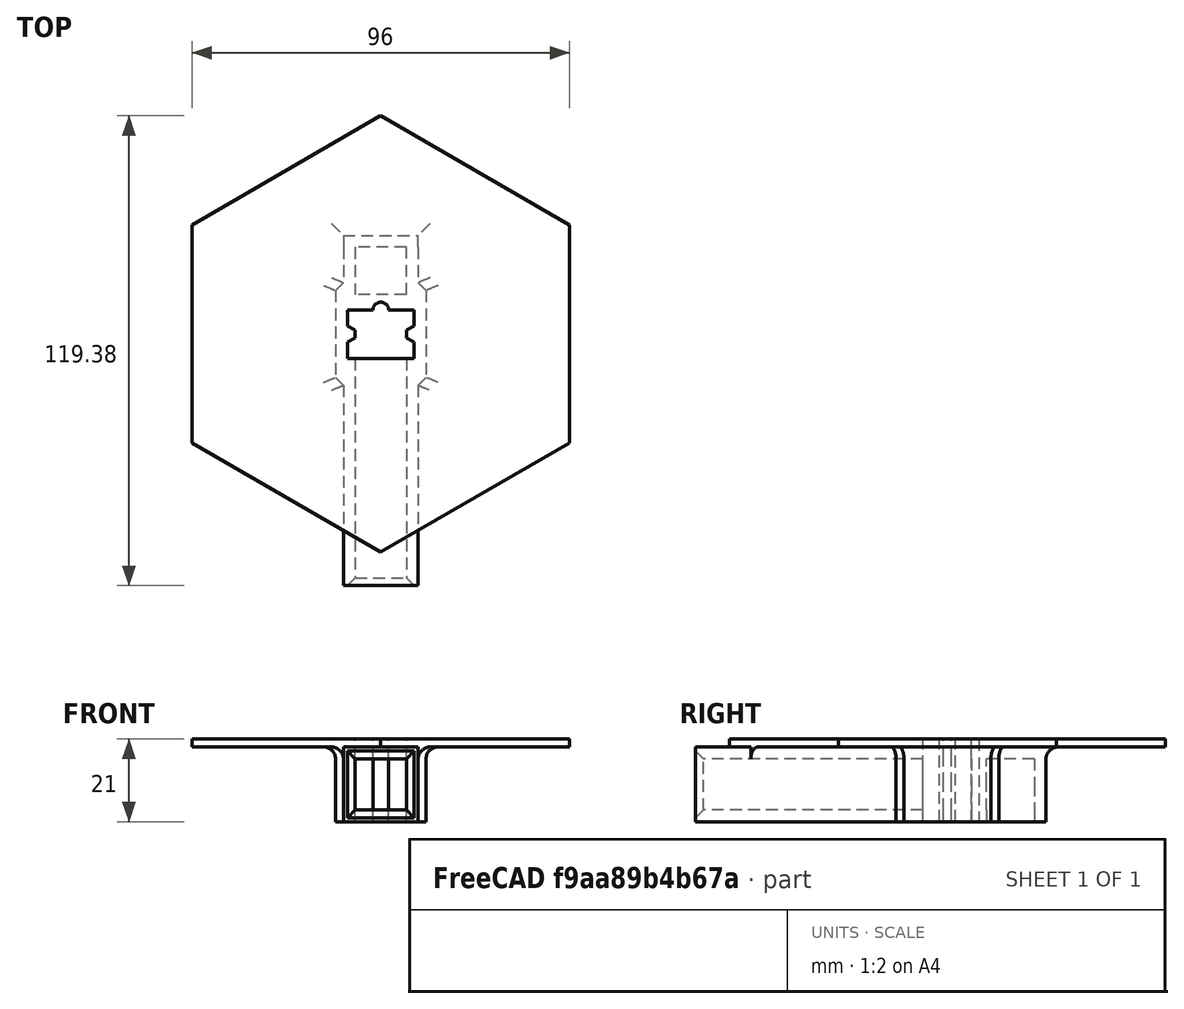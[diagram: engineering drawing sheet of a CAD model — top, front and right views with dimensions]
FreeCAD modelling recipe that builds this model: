
FCSTD DOCUMENT  (FreeCAD 0.21R33771 (Git))
Label: holder
License: All rights reserved
LicenseURL: http://en.wikipedia.org/wiki/All_rights_reserved
objects: Sketcher::SketchObject×7, PartDesign::Pad×5, PartDesign::Pocket×4, Spreadsheet::Sheet×1, PartDesign::Chamfer×1, PartDesign::Fillet×1, PartDesign::Body×1, Mesh::Feature×1
note: 30 computed .brp shape members not serialized (recipe doc carries the construction recipe); baked Part::Feature solids carry a one-line shape summary decoded from their .brp

FEATURE [Sketcher::SketchObject] Sketch
  FullyConstrained = true
  MapMode = 5
  Placement = pos=(0,0,0) rot=(1,0,0;1.5708rad)
  expr: Constraints[25] = Spreadsheet.B1
  sketch-geometry (14):
    g0: LineSegment StartX=-6.5 StartY=6.5 StartZ=0 EndX=6.5 EndY=6.5 EndZ=0
    g1: LineSegment StartX=6.5 StartY=6.5 StartZ=0 EndX=6.5 EndY=-6.5 EndZ=0
    g2: LineSegment StartX=6.5 StartY=-6.5 StartZ=0 EndX=-6.5 EndY=-6.5 EndZ=0
    g3: LineSegment StartX=-6.5 StartY=-6.5 StartZ=0 EndX=-6.5 EndY=6.5 EndZ=0
    g4: LineSegment StartX=-6 StartY=6 StartZ=0 EndX=6 EndY=6 EndZ=0
    g5: LineSegment StartX=6 StartY=6 StartZ=0 EndX=6 EndY=-6 EndZ=0
    g6: LineSegment StartX=6 StartY=-6 StartZ=0 EndX=-6 EndY=-6 EndZ=0
    g7: LineSegment StartX=-6 StartY=-6 StartZ=0 EndX=-6 EndY=6 EndZ=0
    g8: LineSegment StartX=-9.5 StartY=9.5 StartZ=0 EndX=9.5 EndY=9.5 EndZ=0
    g9: LineSegment StartX=9.5 StartY=9.5 StartZ=0 EndX=9.5 EndY=-9.5 EndZ=0
    g10: LineSegment StartX=9.5 StartY=-9.5 StartZ=0 EndX=-9.5 EndY=-9.5 EndZ=0
    g11: LineSegment StartX=-9.5 StartY=-9.5 StartZ=0 EndX=-9.5 EndY=9.5 EndZ=0
    g12: LineSegment StartX=-9.5 StartY=9.5 StartZ=0 EndX=9.5 EndY=-9.5 EndZ=0
    g13: LineSegment StartX=-9.5 StartY=-9.5 StartZ=0 EndX=9.5 EndY=9.5 EndZ=0
  constraints (40):
    c: Coincident(g0,g1)
    c: Coincident(g1,g2)
    c: Coincident(g2,g3)
    c: Coincident(g3,g0)
    c: Horizontal(g0)
    c: Horizontal(g2)
    c: Vertical(g1)
    c: Vertical(g3)
    c: Coincident(g4,g5)
    c: Coincident(g5,g6)
    c: Coincident(g6,g7)
    c: Coincident(g7,g4)
    c: Horizontal(g4)
    c: Horizontal(g6)
    c: Vertical(g5)
    c: Vertical(g7)
    c: Coincident(g8,g9)
    c: Coincident(g9,g10)
    c: Coincident(g10,g11)
    c: Coincident(g11,g8)
    c: Horizontal(g8)
    c: Horizontal(g10)
    c: Vertical(g9)
    c: Vertical(g11)
    c: Equal(g4,g7)
    c: Distance(g4) = 12
    c: Coincident(g12,g8)
    c: Coincident(g12,g9)
    c: PointOnObject(g-1,g12)
    c: PointOnObject(g4,g12)
    c: PointOnObject(g0,g12)
    c: PointOnObject(g5,g12)
    c: PointOnObject(g1,g12)
    c: Distance(g4,g0) = 0.5
    c: Coincident(g13,g10)
    c: Coincident(g13,g8)
    c: PointOnObject(g0,g13)
    c: PointOnObject(g4,g13)
    c: PointOnObject(g-1,g13)
    c: Distance(g0,g8) = 3
FEATURE [Spreadsheet::Sheet] Spreadsheet
  cells = A1='magnet width [mm]; B1=12
FEATURE [PartDesign::Pad] Pad
  Direction = (0,-1,2e-16)
  Length = 86
  Length2 = 10
  Placement = pos=(0,0,0) rot=(1,0,0;1.5708rad)
  Profile = -> Sketch
  ReferenceAxis = -> Sketch [N_Axis]
  Type = 0
  expr: Length = Spreadsheet.B1 * 7 + 2 * 1
FEATURE [Sketcher::SketchObject] Sketch001
  ExternalGeometry = -> [Pad]
  FullyConstrained = true
  MapMode = 5
  Placement = pos=(0,0,0) rot=(1,0,0;1.5708rad)
  Support = -> [XZ_Plane001]
  sketch-geometry (4):
    g0: LineSegment StartX=-9.5 StartY=9.5 StartZ=0 EndX=9.5 EndY=9.5 EndZ=0
    g1: LineSegment StartX=9.5 StartY=9.5 StartZ=0 EndX=9.5 EndY=-9.5 EndZ=0
    g2: LineSegment StartX=9.5 StartY=-9.5 StartZ=0 EndX=-9.5 EndY=-9.5 EndZ=0
    g3: LineSegment StartX=-9.5 StartY=-9.5 StartZ=0 EndX=-9.5 EndY=9.5 EndZ=0
  constraints (10):
    c: Coincident(g0,g1)
    c: Coincident(g1,g2)
    c: Coincident(g2,g3)
    c: Coincident(g3,g0)
    c: Horizontal(g0)
    c: Horizontal(g2)
    c: Vertical(g1)
    c: Vertical(g3)
    c: Coincident(g0,g-4)
    c: Coincident(g1,g-6)
FEATURE [PartDesign::Pad] Pad001
  BaseFeature = -> Pad
  Direction = (0,-1,-2e-16)
  Length = 3
  Length2 = 10
  Placement = pos=(0,0,0) rot=(1,0,0;1.5708rad)
  Profile = -> Sketch001
  ReferenceAxis = -> Sketch001 [N_Axis]
  Reversed = true
  Type = 0
FEATURE [PartDesign::Pad] Pad002
  BaseFeature = -> Pad001
  Direction = (0,-1,-2e-16)
  Length = 16
  Length2 = -12.1
  Placement = pos=(0,0,0) rot=(1,0,0;1.5708rad)
  Profile = -> Sketch001
  ReferenceAxis = -> Sketch001 [N_Axis]
  Type = 4
  expr: Length = Spreadsheet.B1 + 2 + 2
  expr: Length2 = -(Spreadsheet.B1 + 0.1)
FEATURE [Sketcher::SketchObject] Sketch002
  ExternalGeometry = -> [Pad002]
  FullyConstrained = true
  MapMode = 5
  Support = -> [XY_Plane001]
  sketch-geometry (4):
    g0: LineSegment StartX=-6.5 StartY=0 StartZ=0 EndX=6.5 EndY=0 EndZ=0
    g1: LineSegment StartX=6.5 StartY=0 StartZ=0 EndX=6.5 EndY=-12.1 EndZ=0
    g2: LineSegment StartX=6.5 StartY=-12.1 StartZ=0 EndX=-6.5 EndY=-12.1 EndZ=0
    g3: LineSegment StartX=-6.5 StartY=-12.1 StartZ=0 EndX=-6.5 EndY=0 EndZ=0
  constraints (10):
    c: Coincident(g0,g1)
    c: Coincident(g1,g2)
    c: Coincident(g2,g3)
    c: Coincident(g3,g0)
    c: Horizontal(g0)
    c: Vertical(g1)
    c: Vertical(g3)
    c: PointOnObject(g0,g-1)
    c: Coincident(g2,g-4)
    c: Coincident(g1,g-3)
FEATURE [PartDesign::Pocket] Pocket
  BaseFeature = -> Pad002
  Direction = (0,0,-1)
  Length = 16
  Length2 = 5
  Placement = pos=(0,0,0) rot=(1,0,0;1.5708rad)
  Profile = -> Sketch002
  ReferenceAxis = -> Sketch002 [N_Axis]
  Type = 1
FEATURE [Sketcher::SketchObject] Sketch003
  ExternalGeometry = -> [Pocket]
  FullyConstrained = true
  MapMode = 5
  Support = -> [XY_Plane001]
  sketch-geometry (7):
    g0: LineSegment StartX=-6.5 StartY=-16 StartZ=0 EndX=6.5 EndY=-16 EndZ=0
    g1: LineSegment StartX=6.5 StartY=-16 StartZ=0 EndX=6.5 EndY=-29 EndZ=0
    g2: LineSegment StartX=6.5 StartY=-29 StartZ=0 EndX=-6.5 EndY=-29 EndZ=0
    g3: LineSegment StartX=-6.5 StartY=-29 StartZ=0 EndX=-6.5 EndY=-16 EndZ=0
    g4: LineSegment StartX=-6.5 StartY=-28.1 StartZ=0 EndX=6.5 EndY=-28.1 EndZ=0
    g5: LineSegment StartX=-6.5 StartY=-16 StartZ=0 EndX=-6.5 EndY=-28.1 EndZ=0
    g6: LineSegment StartX=6.5 StartY=-16 StartZ=0 EndX=6.5 EndY=-28.1 EndZ=0
  constraints (19):
    c: Coincident(g0,g1)
    c: Coincident(g1,g2)
    c: Coincident(g2,g3)
    c: Coincident(g3,g0)
    c: Horizontal(g0)
    c: Horizontal(g2)
    c: Vertical(g1)
    c: Vertical(g3)
    c: Coincident(g0,g-4)
    c: PointOnObject(g1,g-5)
    c: Equal(g1,g0)
    c: PointOnObject(g4,g3)
    c: PointOnObject(g4,g1)
    c: Horizontal(g4)
    c: Distance(g0,g4) = 12.1
    c: Coincident(g5,g0)
    c: Coincident(g5,g4)
    c: Coincident(g6,g0)
    c: Coincident(g6,g4)
FEATURE [PartDesign::Pocket] Pocket001
  BaseFeature = -> Pocket
  Direction = (0,0,-1)
  Length = 11
  Length2 = 5
  Placement = pos=(0,0,0) rot=(1,0,0;1.5708rad)
  Profile = -> Sketch003
  ReferenceAxis = -> Sketch003 [N_Axis]
  Type = 1
FEATURE [Sketcher::SketchObject] Sketch004
  ExternalGeometry = -> [Pocket001]
  FullyConstrained = true
  MapMode = 5
  Placement = pos=(0,1e-15,9.5) rot=(0,0,1;3.14159rad)
  Support = -> [Pocket001]
  expr: Constraints[18] = Spreadsheet.B1 * 4
  sketch-geometry (9):
    g0: LineSegment StartX=0 StartY=-33.3756 StartZ=0 EndX=48 EndY=-5.66281 EndZ=0
    g1: LineSegment StartX=48 StartY=-5.66281 StartZ=0 EndX=48 EndY=49.7628 EndZ=0
    g2: LineSegment StartX=48 StartY=49.7628 StartZ=0 EndX=-4.9596e-12 EndY=77.4756 EndZ=0
    g3: LineSegment StartX=-4.9596e-12 StartY=77.4756 StartZ=0 EndX=-48 EndY=49.7628 EndZ=0
    g4: LineSegment StartX=-48 StartY=49.7628 StartZ=0 EndX=-48 EndY=-5.66281 EndZ=0
    g5: LineSegment StartX=-48 StartY=-5.66281 StartZ=0 EndX=0 EndY=-33.3756 EndZ=0
    g6: Circle CenterX=0 CenterY=22.05 CenterZ=0 NormalX=0 NormalY=0 NormalZ=1 AngleXU=0 Radius=55.4256
    g7: LineSegment StartX=-6.5 StartY=28.1 StartZ=0 EndX=6.5 EndY=16 EndZ=0
    g8: GeomPoint X=0 Y=22.05 Z=0
  constraints (20):
    c: Coincident(g0,g1)
    c: Coincident(g1,g2)
    c: Coincident(g2,g3)
    c: Coincident(g3,g4)
    c: Coincident(g4,g5)
    c: Coincident(g5,g0)
    c: Equal(g0, g1-g5) x5
    c: PointOnObject(g0,g6)
    c: PointOnObject(g1,g6)
    c: PointOnObject(g2,g6)
    c: PointOnObject(g3,g6)
    c: PointOnObject(g4,g6)
    c: PointOnObject(g5,g6)
    c: PointOnObject(g5,g-2)
    c: Distance(g6,g4) = 48
    c: Coincident(g7,g-4)
    c: PointOnObject(g8,g-2)
    c: PointOnObject(g8,g7)
    c: Coincident(g6,g8)
    c: Coincident(g-3,g7)
FEATURE [PartDesign::Pad] Pad003
  BaseFeature = -> Pocket001
  Direction = (0,3e-16,1)
  Length = 2
  Length2 = 10
  Placement = pos=(0,0,0) rot=(1,0,0;1.5708rad)
  Profile = -> Sketch004
  ReferenceAxis = -> Sketch004 [N_Axis]
  Type = 0
FEATURE [PartDesign::Pocket] Pocket002
  BaseFeature = -> Pad003
  Direction = (0,0,-1)
  Length = 5
  Length2 = 5
  Placement = pos=(0,0,0) rot=(1,0,0;1.5708rad)
  Profile = -> Sketch003
  ReferenceAxis = -> Sketch003 [N_Axis]
  Reversed = true
  Type = 1
FEATURE [PartDesign::Chamfer] Chamfer
  Angle = 45
  Base = -> Pocket002 [Edge80,Edge81,Edge83,Edge82]
  BaseFeature = -> Pocket002
  ChamferType = 0
  FlipDirection = false
  Placement = pos=(0,0,0) rot=(1,0,0;1.5708rad)
  Size = 2
  Size2 = 1
  SupportTransform = false
  UseAllEdges = false
FEATURE [Sketcher::SketchObject] Sketch005
  ExternalGeometry = -> [Chamfer]
  FullyConstrained = false
  MapMode = 5
  Placement = pos=(0,-1e-15,-9.5) rot=(1,0,0;3.14159rad)
  Support = -> [Chamfer]
  sketch-geometry (41):
    g0: LineSegment StartX=-6.5 StartY=28.1 StartZ=0 EndX=6.5 EndY=16 EndZ=0
    g1: LineSegment StartX=-6.5 StartY=16 StartZ=0 EndX=6.5 EndY=28.1 EndZ=0
    g2: GeomPoint X=1.7e-15 Y=22.05 Z=0
    g3: LineSegment StartX=1.7e-15 StartY=22.05 StartZ=0 EndX=-6.5 EndY=22.05 EndZ=0
    g4: LineSegment StartX=1.7e-15 StartY=22.05 StartZ=0 EndX=6.5 EndY=22.05 EndZ=0
    g5: LineSegment StartX=1.7e-15 StartY=22.05 StartZ=0 EndX=1.7e-15 EndY=16 EndZ=0
    g6: Circle CenterX=1.7e-15 CenterY=16 CenterZ=0 NormalX=0 NormalY=0 NormalZ=1 AngleXU=0 Radius=2
    g7: LineSegment StartX=-9.5 StartY=16 StartZ=0 EndX=-6.5 EndY=16 EndZ=0
    g8: LineSegment StartX=-8.5 StartY=16 StartZ=0 EndX=8.5 EndY=16 EndZ=0
    g9: LineSegment StartX=8.5 StartY=16 StartZ=0 EndX=8.5 EndY=28.3 EndZ=0
    g10: LineSegment StartX=8.5 StartY=28.3 StartZ=0 EndX=-8.5 EndY=28.3 EndZ=0
    g11: LineSegment StartX=-8.5 StartY=28.3 StartZ=0 EndX=-8.5 EndY=16 EndZ=0
    g12: LineSegment StartX=-6.5 StartY=22.05 StartZ=0 EndX=-8.5 EndY=22.05 EndZ=0
    g13: LineSegment StartX=6.5 StartY=22.05 StartZ=0 EndX=8.5 EndY=22.05 EndZ=0
    g14: LineSegment StartX=6.5 StartY=28.1 StartZ=0 EndX=6.5 EndY=28.3 EndZ=0
    g15: LineSegment StartX=1.7e-15 StartY=16 StartZ=0 EndX=-1.65657 EndY=17.1206 EndZ=0
    g16: Circle CenterX=-6.5 CenterY=22.05 CenterZ=0 NormalX=0 NormalY=0 NormalZ=1 AngleXU=0 Radius=1
    g17: Circle CenterX=6.5 CenterY=22.05 CenterZ=0 NormalX=0 NormalY=0 NormalZ=1 AngleXU=0 Radius=1
    g18: GeomPoint X=-6.5 Y=23.05 Z=0
    g19: GeomPoint X=6.5 Y=23.05 Z=0
    g20: GeomPoint X=-6.5 Y=21.05 Z=0
    g21: GeomPoint X=6.5 Y=21.05 Z=0
    g22: Circle CenterX=-8.5 CenterY=22.05 CenterZ=0 NormalX=0 NormalY=0 NormalZ=1 AngleXU=0 Radius=2
    g23: Circle CenterX=8.5 CenterY=22.05 CenterZ=0 NormalX=0 NormalY=0 NormalZ=1 AngleXU=0 Radius=2
    g24: GeomPoint X=-8.5 Y=24.05 Z=0
    g25: GeomPoint X=-8.5 Y=20.05 Z=0
    g26: GeomPoint X=8.5 Y=24.05 Z=0
    g27: GeomPoint X=8.5 Y=20.05 Z=0
    g28: LineSegment StartX=-8.5 StartY=24.05 StartZ=0 EndX=-6.5 EndY=23.05 EndZ=0
    g29: LineSegment StartX=-6.5 StartY=21.05 StartZ=0 EndX=-8.5 EndY=20.05 EndZ=0
    g30: LineSegment StartX=-8.5 StartY=28.3 StartZ=0 EndX=-8.5 EndY=24.05 EndZ=0
    g31: LineSegment StartX=-8.5 StartY=20.05 StartZ=0 EndX=-8.5 EndY=16 EndZ=0
    g32: LineSegment StartX=6.5 StartY=23.05 StartZ=0 EndX=8.5 EndY=24.05 EndZ=0
    g33: LineSegment StartX=6.5 StartY=21.05 StartZ=0 EndX=8.5 EndY=20.05 EndZ=0
    g34: LineSegment StartX=6.5 StartY=23.05 StartZ=0 EndX=6.5 EndY=21.05 EndZ=0
    g35: LineSegment StartX=-6.5 StartY=23.05 StartZ=0 EndX=-6.5 EndY=21.05 EndZ=0
    g36: LineSegment StartX=8.5 StartY=24.05 StartZ=0 EndX=8.5 EndY=28.3 EndZ=0
    g37: LineSegment StartX=8.5 StartY=20.05 StartZ=0 EndX=8.5 EndY=16 EndZ=0
    g38: LineSegment StartX=-8.5 StartY=16 StartZ=0 EndX=-2 EndY=16 EndZ=0
    g39: LineSegment StartX=2 StartY=16 StartZ=0 EndX=8.5 EndY=16 EndZ=0
    g40: ArcOfCircle CenterX=1.7e-15 CenterY=16 CenterZ=0 NormalX=0 NormalY=0 NormalZ=1 AngleXU=0 Radius=2 StartAngle=3.14159 EndAngle=6.28319
  constraints (95):
    c: PointOnObject(g2,g0)
    c: PointOnObject(g2,g1)
    c: Coincident(g3,g2)
    c: PointOnObject(g3,g-5)
    c: Horizontal(g3)
    c: Coincident(g4,g2)
    c: PointOnObject(g4,g-7)
    c: Horizontal(g4)
    c: Coincident(g5,g2)
    c: PointOnObject(g5,g-8)
    c: Vertical(g5)
    c: Coincident(g6,g5)
    c: Coincident(g7,g-3)
    c: Coincident(g7,g1)
    c: Coincident(g8,g9)
    c: Coincident(g9,g10)
    c: Coincident(g10,g11)
    c: Coincident(g11,g8)
    c: Horizontal(g8)
    c: Horizontal(g10)
    c: Vertical(g9)
    c: Vertical(g11)
    c: PointOnObject(g8,g7)
    c: Coincident(g12,g3)
    c: PointOnObject(g12,g11)
    c: Horizontal(g12)
    c: Coincident(g13,g4)
    c: PointOnObject(g13,g9)
    c: Horizontal(g13)
    c: Coincident(g14,g1)
    c: PointOnObject(g14,g10)
    c: Vertical(g14)
    c: Radius(g6) = 2
    c: Coincident(g0,g-8)
    c: Coincident(g1,g-7)
    c: Coincident(g0,g-6)
    c: Coincident(g1,g-8)
    c: Coincident(g15,g6)
    c: PointOnObject(g15,g6)
    c: Equal(g12,g13)
    c: Equal(g13,g15)
    c: Distance(g14) = 0.2
    c: Coincident(g16,g3)
    c: Coincident(g17,g4)
    c: Radius(g17) = 1
    c: Radius(g16) = 1
    c: PointOnObject(g18,g-5)
    c: PointOnObject(g19,g-7)
    c: PointOnObject(g20,g-5)
    c: PointOnObject(g21,g-7)
    c: PointOnObject(g18,g16)
    c: PointOnObject(g20,g16)
    c: PointOnObject(g21,g17)
    c: PointOnObject(g19,g17)
    c: Coincident(g22,g12)
    c: Coincident(g23,g13)
    c: Equal(g22,g23)
    c: Equal(g23,g6)
    c: PointOnObject(g24,g22)
    c: PointOnObject(g25,g22)
    c: PointOnObject(g26,g23)
    c: PointOnObject(g27,g23)
    c: PointOnObject(g26,g9)
    c: PointOnObject(g27,g9)
    c: PointOnObject(g24,g11)
    c: PointOnObject(g25,g11)
    c: Coincident(g28,g24)
    c: Coincident(g28,g18)
    c: Coincident(g29,g20)
    c: Coincident(g29,g25)
    c: Coincident(g30,g10)
    c: Coincident(g30,g28)
    c: Coincident(g31,g29)
    c: Coincident(g31,g8)
    c: Coincident(g32,g19)
    c: Coincident(g32,g26)
    c: Coincident(g33,g21)
    c: Coincident(g33,g27)
    c: Coincident(g34,g32)
    c: Coincident(g34,g33)
    c: Coincident(g35,g28)
    c: Coincident(g35,g29)
    c: Coincident(g36,g32)
    c: Coincident(g36,g10)
    c: Coincident(g37,g33)
    c: Coincident(g37,g8)
    c: Coincident(g38,g31)
    c: PointOnObject(g38,g6)
    c: PointOnObject(g39,g6)
    c: Coincident(g39,g37)
    c: Horizontal(g38)
    c: Horizontal(g39)
    c: Coincident(g40,g5)
    c: Coincident(g40,g38)
    c: PointOnObject(g40,g8)
FEATURE [Sketcher::SketchObject] Sketch006
  ExternalGeometry = -> [Chamfer]
  FullyConstrained = false
  MapMode = 5
  Placement = pos=(0,-1e-15,-9.5) rot=(1,0,0;3.14159rad)
  Support = -> [Chamfer]
  sketch-geometry (32):
    g0: Circle CenterX=-6.5 CenterY=16 CenterZ=0 NormalX=0 NormalY=0 NormalZ=1 AngleXU=0 Radius=5
    g1: Circle CenterX=6.5 CenterY=16 CenterZ=0 NormalX=0 NormalY=0 NormalZ=1 AngleXU=0 Radius=5
    g2: Circle CenterX=6.5 CenterY=28.1 CenterZ=0 NormalX=0 NormalY=0 NormalZ=1 AngleXU=0 Radius=5
    g3: Circle CenterX=-6.5 CenterY=28.1 CenterZ=0 NormalX=0 NormalY=0 NormalZ=1 AngleXU=0 Radius=5
    g4: LineSegment StartX=-6.5 StartY=16 StartZ=0 EndX=-6.5 EndY=11 EndZ=0
    g5: LineSegment StartX=6.5 StartY=16 StartZ=0 EndX=6.5 EndY=11 EndZ=0
    g6: LineSegment StartX=-6.5 StartY=11 StartZ=0 EndX=-9.5 EndY=11 EndZ=0
    g7: LineSegment StartX=6.5 StartY=11 StartZ=0 EndX=9.5 EndY=11 EndZ=0
    g8: LineSegment StartX=-6.5 StartY=28.1 StartZ=0 EndX=-6.5 EndY=33.1 EndZ=0
    g9: LineSegment StartX=6.5 StartY=28.1 StartZ=0 EndX=6.5 EndY=33.1 EndZ=0
    g10: LineSegment StartX=6.5 StartY=33.1 StartZ=0 EndX=9.5 EndY=33.1 EndZ=0
    g11: LineSegment StartX=-6.5 StartY=33.1 StartZ=0 EndX=-9.5 EndY=33.1 EndZ=0
    g12: LineSegment StartX=-9.5 StartY=11 StartZ=0 EndX=-11.5 EndY=11 EndZ=0
    g13: LineSegment StartX=-11.5 StartY=11 StartZ=0 EndX=-11.5 EndY=33.1 EndZ=0
    g14: LineSegment StartX=-11.5 StartY=33.1 StartZ=0 EndX=-9.5 EndY=33.1 EndZ=0
    g15: LineSegment StartX=-9.5 StartY=33.1 StartZ=0 EndX=-9.5 EndY=11 EndZ=0
    g16: LineSegment StartX=-6.5 StartY=28.1 StartZ=0 EndX=-11.5 EndY=28.1 EndZ=0
    g17: LineSegment StartX=6.5 StartY=28.1 StartZ=0 EndX=11.5 EndY=28.1 EndZ=0
    g18: LineSegment StartX=11.5 StartY=11 StartZ=0 EndX=11.5 EndY=33.1 EndZ=0
    g19: LineSegment StartX=11.5 StartY=33.1 StartZ=0 EndX=9.5 EndY=33.1 EndZ=0
    g20: LineSegment StartX=9.5 StartY=33.1 StartZ=0 EndX=9.5 EndY=11 EndZ=0
    g21: LineSegment StartX=-9.5 StartY=11 StartZ=0 EndX=-9.5 EndY=9 EndZ=0
    g22: LineSegment StartX=9.5 StartY=11 StartZ=0 EndX=9.5 EndY=9 EndZ=0
    g23: LineSegment StartX=9.5 StartY=9 StartZ=0 EndX=11.5 EndY=11 EndZ=0
    g24: LineSegment StartX=-11.5 StartY=11 StartZ=0 EndX=-9.5 EndY=9 EndZ=0
    g25: LineSegment StartX=9.5 StartY=9 StartZ=0 EndX=9.5 EndY=11 EndZ=0
    g26: LineSegment StartX=9.5 StartY=11 StartZ=0 EndX=11.5 EndY=11 EndZ=0
    g27: LineSegment StartX=-9.5 StartY=9 StartZ=0 EndX=-9.5 EndY=11 EndZ=0
    g28: LineSegment StartX=-11.5 StartY=33.1 StartZ=0 EndX=-9.5 EndY=35.1 EndZ=0
    g29: LineSegment StartX=11.5 StartY=33.1 StartZ=0 EndX=9.5 EndY=35.1 EndZ=0
    g30: LineSegment StartX=-9.5 StartY=35.1 StartZ=0 EndX=-9.5 EndY=33.1 EndZ=0
    g31: LineSegment StartX=9.5 StartY=35.1 StartZ=0 EndX=9.5 EndY=33.1 EndZ=0
  constraints (81):
    c: Coincident(g0,g-5)
    c: Radius(g0) = 5
    c: Coincident(g1,g-6)
    c: Coincident(g2,g-6)
    c: Coincident(g3,g-5)
    c: Equal(g3,g2)
    c: Equal(g2,g1)
    c: Equal(g1,g0)
    c: Coincident(g4,g0)
    c: PointOnObject(g4,g0)
    c: Vertical(g4)
    c: Coincident(g5,g1)
    c: PointOnObject(g5,g1)
    c: Vertical(g5)
    c: Coincident(g6,g4)
    c: PointOnObject(g6,g-7)
    c: Coincident(g7,g5)
    c: Horizontal(g6)
    c: Horizontal(g7)
    c: Coincident(g8,g3)
    c: PointOnObject(g8,g3)
    c: Vertical(g8)
    c: Coincident(g9,g2)
    c: PointOnObject(g9,g2)
    c: Vertical(g9)
    c: Coincident(g10,g9)
    c: Horizontal(g10)
    c: Coincident(g11,g8)
    c: Horizontal(g11)
    c: Coincident(g12,g13)
    c: Coincident(g13,g14)
    c: Coincident(g14,g15)
    c: Coincident(g15,g12)
    c: Horizontal(g12)
    c: Horizontal(g14)
    c: Vertical(g13)
    c: Vertical(g15)
    c: Coincident(g12,g6)
    c: Coincident(g14,g11)
    c: Coincident(g16,g3)
    c: PointOnObject(g16,g3)
    c: Horizontal(g16)
    c: PointOnObject(g16,g13)
    c: Coincident(g17,g2)
    c: PointOnObject(g17,g2)
    c: Horizontal(g17)
    c: Coincident(g18,g19)
    c: Coincident(g19,g20)
    c: Horizontal(g19)
    c: Vertical(g18)
    c: Vertical(g20)
    c: Coincident(g19,g10)
    c: PointOnObject(g17,g18)
    c: Coincident(g21,g12)
    c: PointOnObject(g21,g-7)
    c: Equal(g21,g12)
    c: PointOnObject(g22,g-10)
    c: Coincident(g23,g22)
    c: Coincident(g24,g12)
    c: Coincident(g24,g21)
    c: Coincident(g25,g23)
    c: Vertical(g25)
    c: Coincident(g23,g18)
    c: Coincident(g26,g20)
    c: Coincident(g26,g18)
    c: Equal(g25,g26)
    c: Horizontal(g26)
    c: Coincident(g20,g25)
    c: Coincident(g20,g7)
    c: Coincident(g27,g24)
    c: Coincident(g27,g15)
    c: Coincident(g28,g13)
    c: PointOnObject(g28,g-3)
    c: Coincident(g29,g18)
    c: PointOnObject(g29,g-4)
    c: Coincident(g30,g28)
    c: Coincident(g30,g15)
    c: Coincident(g31,g29)
    c: Coincident(g31,g20)
    c: Equal(g31,g19)
    c: Equal(g30,g14)
FEATURE [PartDesign::Pad] Pad004
  BaseFeature = -> Chamfer
  Direction = (0,-6e-16,-1)
  Length = 9
  Length2 = 10
  Placement = pos=(0,0,0) rot=(1,0,0;1.5708rad)
  Profile = -> Sketch006
  ReferenceAxis = -> Sketch006 [N_Axis]
  Reversed = true
  Type = 3
  UpToFace = -> Chamfer [Face17]
FEATURE [PartDesign::Pocket] Pocket003
  BaseFeature = -> Pad004
  Direction = (0,6e-16,1)
  Length = 5
  Length2 = 5
  Placement = pos=(0,0,0) rot=(1,0,0;1.5708rad)
  Profile = -> Sketch005
  ReferenceAxis = -> Sketch005 [N_Axis]
  Type = 1
FEATURE [PartDesign::Fillet] Fillet
  Base = -> Pocket003 [Edge69,Edge70,Edge71,Edge72,Edge23,Edge66,Edge65,Edge64,Edge63,Edge60,Edge67,Edge68,Edge43]
  BaseFeature = -> Pocket003
  Placement = pos=(0,0,0) rot=(1,0,0;1.5708rad)
  Radius = 3
  SupportTransform = false
  UseAllEdges = false
FEATURE [PartDesign::Body] Body
  Group = -> [Sketch,Pad,Sketch001,Pad001,Pad002,Sketch002,Pocket,Sketch003,Pocket001,Sketch004,Pad003,Pocket002,Chamfer,Sketch006,Pad004,Sketch005,Pocket003,Fillet]
  Origin = -> Origin001
  Tip = -> Fillet
FEATURE [Mesh::Feature] Mesh001  label="print-holder"
